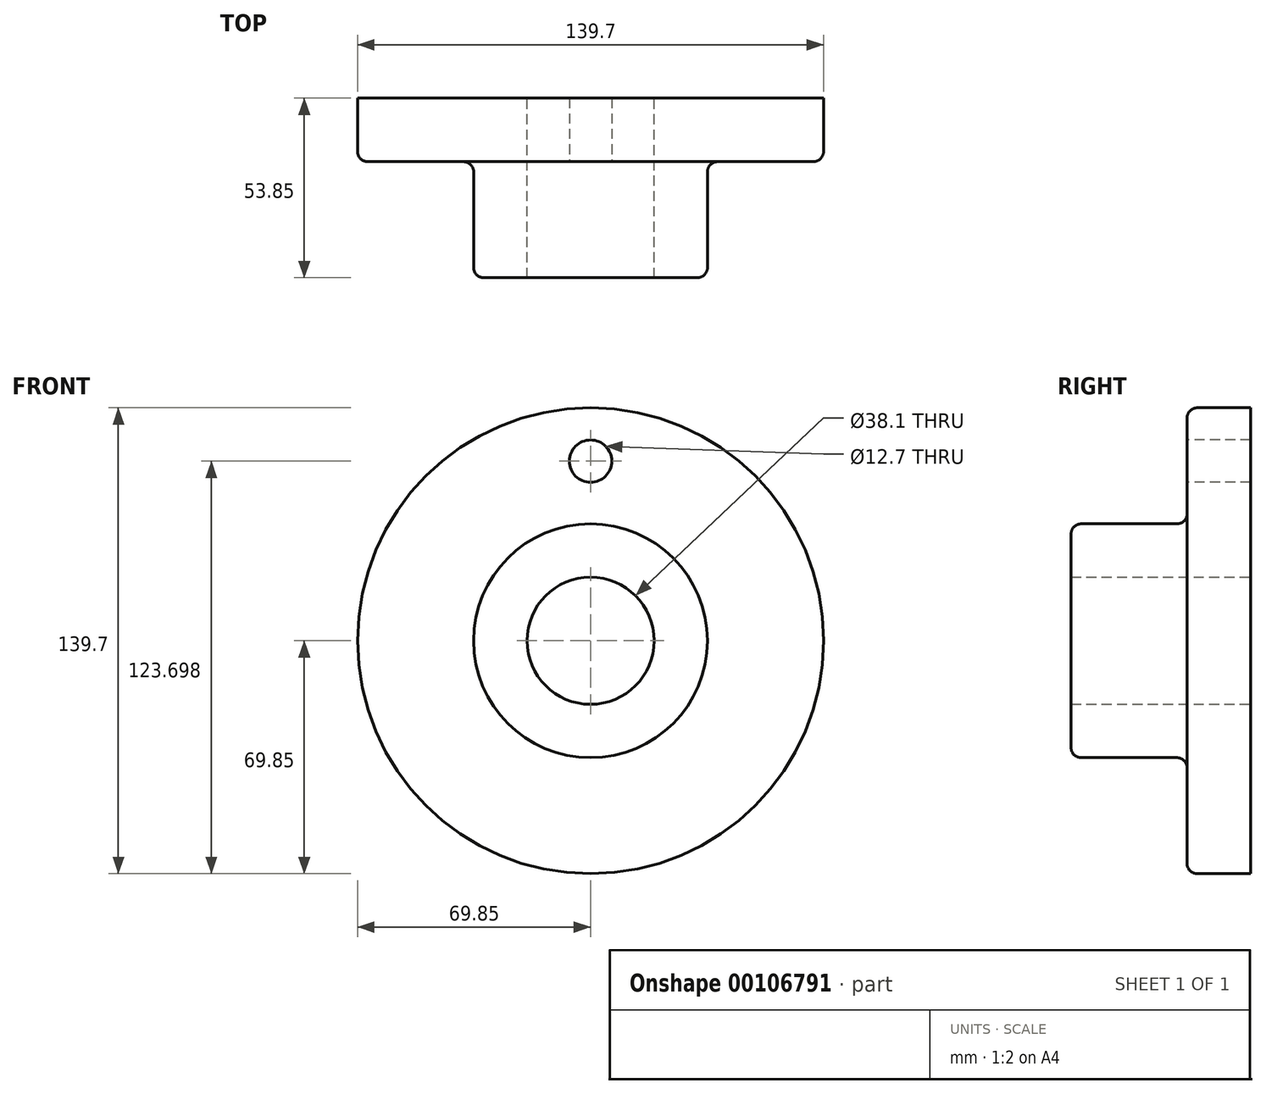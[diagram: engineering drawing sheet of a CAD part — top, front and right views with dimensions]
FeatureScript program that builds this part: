
annotation { "Feature Type Name" : "Feature", "Feature Type Description" : "" }
export const myFeature = defineFeature(function(context is Context, id is Id, definition is map)
    precondition{}
    {
        {
            var Q0;
            Q0=qCreatedBy(makeId("Right.planeOp"),FACE);
            var sketch = newSketch(context, id + "F0", { "sketchPlane" : qUnion([Q0])});
            skLineSegment(sketch, "E0", {"start": v(25.48, 0) * mm, "end": v(-135.87, 0) * mm, "construction": true});
            skLineSegment(sketch, "E1", {"start": v(0, 19.05) * mm, "end": v(-53.85, 19.05) * mm});
            skLineSegment(sketch, "E2", {"start": v(-53.85, 19.05) * mm, "end": v(-53.85, 35.05) * mm});
            skLineSegment(sketch, "E3", {"start": v(-53.85, 35.05) * mm, "end": v(-19.05, 35.05) * mm});
            skLineSegment(sketch, "E4", {"start": v(-19.05, 35.05) * mm, "end": v(-19.05, 69.85) * mm});
            skLineSegment(sketch, "E5", {"start": v(-19.05, 69.85) * mm, "end": v(0, 69.85) * mm});
            skLineSegment(sketch, "E6", {"start": v(0, 69.85) * mm, "end": v(0, 19.05) * mm});
            skSolve(sketch);
        }
        {
            var Q0;
            Q0=makeQuery(id+"F0.imprint","IMPRINT",FACE,{"disambiguationData":[TD([[makeQuery(id+"F0.imprint","IMPRINT",EDGE,{"derivedFrom":sQuery(id+"F0.wireOp",EDGE,"E1")}),-1.0]])]});
            var Q1;
            Q1=sQuery(id+"F0.wireOp",EDGE,"E0");
            revolve(context, id + "F1", {"entities" : qUnion([Q0]), "axis" : qUnion([Q1]), "revolveType" : RevolveType.FULL});
        }
        {
            var Q0;
            Q0=makeQuery(id+"F1.opRevolve","SWEPT_FACE",FACE,{"disambiguationData":[OSD([sQuery(id+"F0.wireOp",EDGE,"E4")])]});
            var sketch = newSketch(context, id + "F2", { "sketchPlane" : qUnion([Q0])});
            skCircle(sketch, "E7", {"center": v(0, 53.85) * mm, "radius": 6.35 * mm});
            skCircle(sketch, "E8", {"center": v(0, 0) * mm, "radius": 53.85 * mm, "construction": true});
            skSolve(sketch);
        }
        {
            var Q0;
            Q0=makeQuery(id+"F2.imprint","IMPRINT",FACE,{"disambiguationData":[TD([[makeQuery(id+"F2.imprint","IMPRINT",EDGE,{"derivedFrom":sQuery(id+"F2.wireOp",EDGE,"E7")}),1.0]])]});
            extrude(context, id + "F3", {"entities" : qUnion([Q0]), "operationType" : NewBodyOperationType.REMOVE, "endBound" : BoundingType.THROUGH_ALL, "oppositeDirection" : true, "depth" : 25.4 * mm});
        }
        {
            var Q0;
            Q0=makeQuery(id+"F1.opRevolve","SWEPT_EDGE",EDGE,{"disambiguationData":[OSD([sQuery(id+"F0.wireOp",EDGE,"E4"),sQuery(id+"F0.wireOp",EDGE,"E5")])]});
            var Q1;
            Q1=makeQuery(id+"F1.opRevolve","SWEPT_EDGE",EDGE,{"disambiguationData":[OSD([sQuery(id+"F0.wireOp",EDGE,"E3"),sQuery(id+"F0.wireOp",EDGE,"E4")])]});
            var Q2;
            Q2=makeQuery(id+"F1.opRevolve","SWEPT_EDGE",EDGE,{"disambiguationData":[OSD([sQuery(id+"F0.wireOp",EDGE,"E2"),sQuery(id+"F0.wireOp",EDGE,"E3")])]});
            fillet(context, id + "F4", {"entities" : qUnion([Q0, Q1, Q2]), "radius" : 3.05 * mm, "tangentPropagation" : true, "allowEdgeOverflow" : false});
        }
    });
